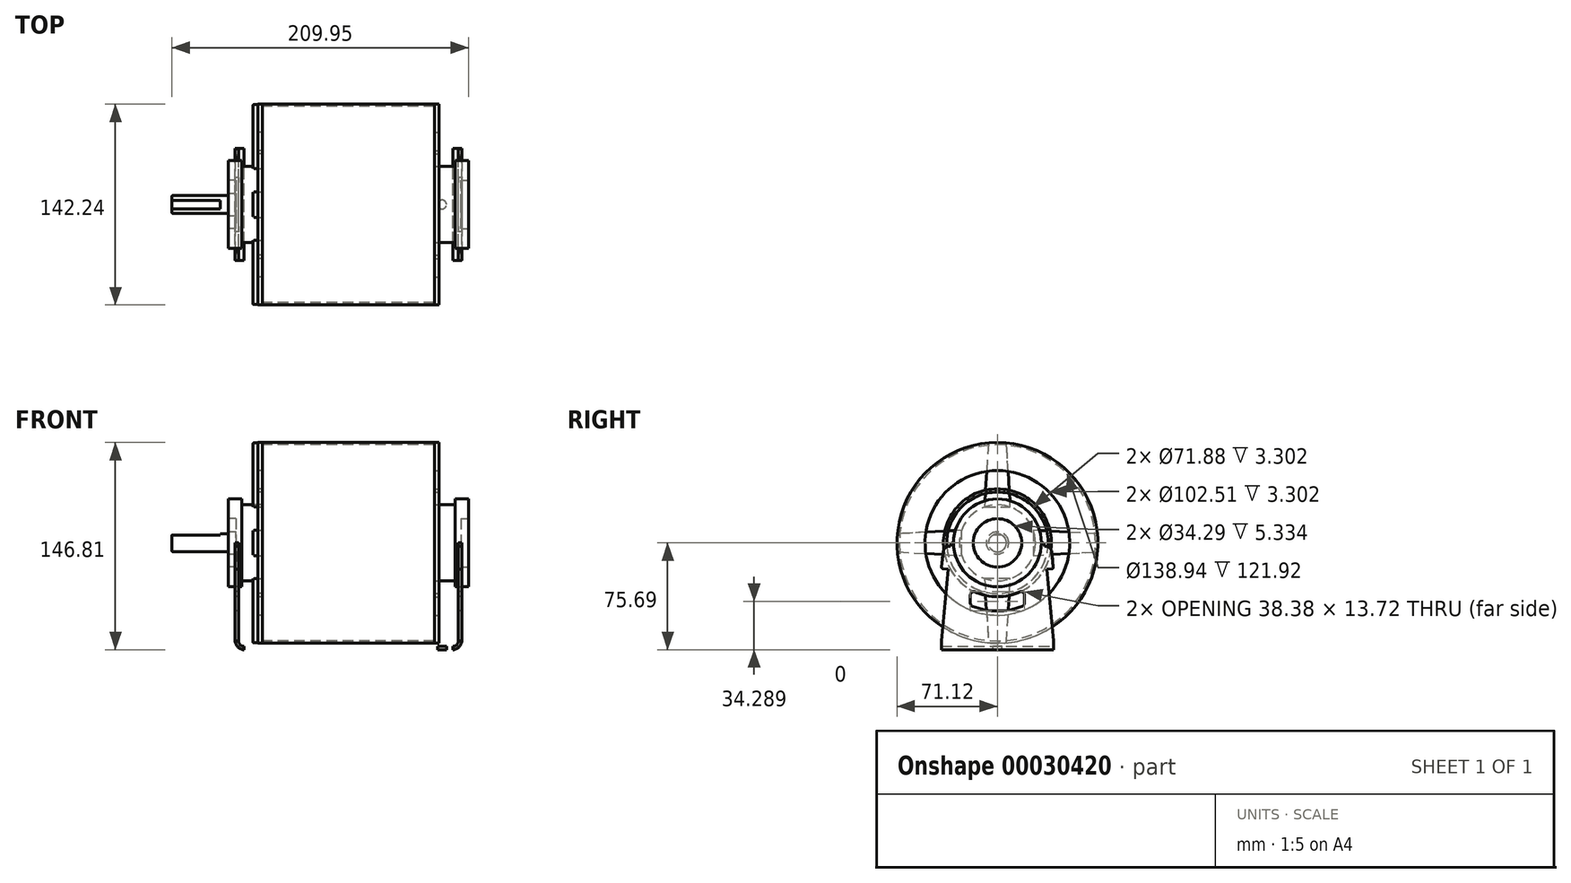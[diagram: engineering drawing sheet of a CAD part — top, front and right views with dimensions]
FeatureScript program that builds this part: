
annotation { "Feature Type Name" : "Feature", "Feature Type Description" : "" }
export const myFeature = defineFeature(function(context is Context, id is Id, definition is map)
    precondition{}
    {
        {
            var Q0;
            Q0=qCreatedBy(makeId("Right.planeOp"),FACE);
            var sketch = newSketch(context, id + "F0", { "sketchPlane" : qUnion([Q0])});
            skCircle(sketch, "E0", {"center": v(0, 0) * mm, "radius": 71.12 * mm});
            skCircle(sketch, "E1.0", {"center": v(0, 0) * mm, "radius": 69.47 * mm});
            skSolve(sketch);
        }
        {
            var Q0;
            Q0=makeQuery(id+"F0.imprint","IMPRINT",FACE,{"disambiguationData":[TD([[makeQuery(id+"F0.imprint","IMPRINT",EDGE,{"derivedFrom":sQuery(id+"F0.wireOp",EDGE,"E0")}),1.0]])]});
            extrude(context, id + "F1", {"entities" : qUnion([Q0]), "depth" : 121.92 * mm});
        }
        {
            var Q0;
            Q0=qCreatedBy(makeId("Front.planeOp"),FACE);
            var sketch = newSketch(context, id + "F2", { "sketchPlane" : qUnion([Q0])});
            skLineSegment(sketch, "E2", {"start": v(0, 0) * mm, "end": v(0, 71.12) * mm});
            skLineSegment(sketch, "E3", {"start": v(0, 71.12) * mm, "end": v(-3.3, 71.12) * mm});
            skLineSegment(sketch, "E4", {"start": v(-3.3, 71.12) * mm, "end": v(-3.3, 26.92) * mm});
            skLineSegment(sketch, "E5", {"start": v(-3.3, 26.92) * mm, "end": v(-14.48, 26.92) * mm});
            skLineSegment(sketch, "E6", {"start": v(-14.48, 26.92) * mm, "end": v(-14.48, 31.12) * mm});
            skLineSegment(sketch, "E7", {"start": v(-14.48, 31.12) * mm, "end": v(-24, 31.12) * mm});
            skLineSegment(sketch, "E8", {"start": v(-24, 31.12) * mm, "end": v(-24, 17.15) * mm});
            skLineSegment(sketch, "E9", {"start": v(-24, 17.15) * mm, "end": v(-18.67, 17.15) * mm});
            skLineSegment(sketch, "E10", {"start": v(-18.67, 17.15) * mm, "end": v(-18.67, 0) * mm});
            skLineSegment(sketch, "E11", {"start": v(-18.67, 0) * mm, "end": v(0, 0) * mm});
            skSolve(sketch);
        }
        {
            var Q0;
            Q0=makeQuery(id+"F2.imprint","IMPRINT",FACE,{"disambiguationData":[TD([[makeQuery(id+"F2.imprint","IMPRINT",EDGE,{"derivedFrom":sQuery(id+"F2.wireOp",EDGE,"E2")}),1.0]])]});
            var Q1;
            Q1=sQuery(id+"F2.wireOp",EDGE,"E11");
            revolve(context, id + "F3", {"entities" : qUnion([Q0]), "axis" : qUnion([Q1]), "revolveType" : RevolveType.FULL});
        }
        {
            var Q0;
            Q0=makeQuery(id+"F3.opRevolve","SWEPT_FACE",FACE,{"disambiguationData":[OSD([sQuery(id+"F2.wireOp",EDGE,"E4")])]});
            var sketch = newSketch(context, id + "F4", { "sketchPlane" : qUnion([Q0])});
            skCircle(sketch, "E12", {"center": v(0, 0) * mm, "radius": 51.26 * mm});
            skCircle(sketch, "E13", {"center": v(0, 0) * mm, "radius": 38.23 * mm});
            skCircle(sketch, "E14.0", {"center": v(0, 0) * mm, "radius": 35.94 * mm});
            skSolve(sketch);
        }
        {
            var Q0;
            Q0=qSketchRegion(id+"F4",true);
            var Q1;
            Q1=makeQuery(id+"F4.imprint","IMPRINT",FACE,{"disambiguationData":[TD([[makeQuery(id+"F4.imprint","IMPRINT",EDGE,{"derivedFrom":sQuery(id+"F4.wireOp",EDGE,"E14.0")}),1.0]])]});
            extrude(context, id + "F5", {"entities" : qUnion([Q0, Q1]), "operationType" : NewBodyOperationType.REMOVE, "endBound" : BoundingType.THROUGH_ALL, "oppositeDirection" : true, "depth" : 25.4 * mm});
        }
        {
            var Q0;
            Q0=qCreatedBy(makeId("Right.planeOp"),FACE);
            var sketch = newSketch(context, id + "F6", { "sketchPlane" : qUnion([Q0])});
            skLineSegment(sketch, "E15", {"start": v(0, 0) * mm, "end": v(0, 71.12) * mm, "construction": true});
            skPoint(sketch, "E16.rect.middle", {"position": v(0, 71.12) * mm});
            skCircle(sketch, "E17", {"center": v(0, 26.92) * mm, "radius": 9.2 * mm, "construction": true});
            skCircle(sketch, "E18.0", {"center": v(0, 0) * mm, "radius": 71.12 * mm, "construction": true});
            skCircle(sketch, "E19", {"center": v(0, 71.12) * mm, "radius": 6.35 * mm, "construction": true});
            skLineSegment(sketch, "E20", {"start": v(9.07, 25.35) * mm, "end": v(6.38, 70.83) * mm});
            skLineSegment(sketch, "E21", {"start": v(6.38, 70.83) * mm, "end": v(-6.38, 70.83) * mm});
            skLineSegment(sketch, "E22", {"start": v(-6.38, 70.83) * mm, "end": v(-9.07, 25.35) * mm});
            skLineSegment(sketch, "E23", {"start": v(-9.07, 25.35) * mm, "end": v(9.07, 25.35) * mm});
            skCircle(sketch, "E24.0", {"center": v(0, 0) * mm, "radius": 26.92 * mm, "construction": true});
            skSolve(sketch);
        }
        {
            var Q0;
            {var subQ3=sQuery(id+"F6.wireOp",EDGE,"E20");Q0=makeQuery(id+"F6.imprint","IMPRINT",FACE,{"disambiguationData":[TD([[makeQuery(id+"F6.imprint","IMPRINT",EDGE,{"derivedFrom":subQ3}),1.0]])]});}
            extrude(context, id + "F7", {"entities" : qUnion([Q0]), "oppositeDirection" : true, "depth" : 6.6 * mm});
        }
        {
            var Q0;
            Q0=makeQuery(id+"F7.opExtrude","CAP_EDGE",EDGE,{"disambiguationData":[OSD([sQuery(id+"F6.wireOp",EDGE,"E20")])],"isStart":false});
            var Q1;
            Q1=makeQuery(id+"F7.opExtrude","CAP_EDGE",EDGE,{"disambiguationData":[OSD([sQuery(id+"F6.wireOp",EDGE,"E21")])],"isStart":false});
            var Q2;
            Q2=makeQuery(id+"F7.opExtrude","CAP_EDGE",EDGE,{"disambiguationData":[OSD([sQuery(id+"F6.wireOp",EDGE,"E22")])],"isStart":false});
            var Q3;
            Q3=makeQuery(id+"F7.opExtrude","SWEPT_EDGE",EDGE,{"disambiguationData":[OSD([sQuery(id+"F2.wireOp",EDGE,"E3"),sQuery(id+"F2.wireOp",EDGE,"E4"),sQuery(id+"F6.wireOp",EDGE,"E20"),sQuery(id+"F6.wireOp",EDGE,"E21")])]});
            var Q4;
            Q4=makeQuery(id+"F7.opExtrude","SWEPT_EDGE",EDGE,{"disambiguationData":[OSD([sQuery(id+"F2.wireOp",EDGE,"E3"),sQuery(id+"F2.wireOp",EDGE,"E4"),sQuery(id+"F6.wireOp",EDGE,"E21"),sQuery(id+"F6.wireOp",EDGE,"E22")])]});
            fillet(context, id + "F8", {"entities" : qUnion([Q0, Q1, Q2, Q3, Q4]), "radius" : 0.5 * mm, "tangentPropagation" : true, "allowEdgeOverflow" : false});
        }
        {
            var Q0;
            Q0=makeQuery(id+"F7.opExtrude","SWEPT_BODY",BODY,{"disambiguationData":[OSD([sQuery(id+"F2.wireOp",EDGE,"E4"),sQuery(id+"F2.wireOp",EDGE,"E5"),sQuery(id+"F6.wireOp",EDGE,"E20"),sQuery(id+"F6.wireOp",EDGE,"E21"),sQuery(id+"F6.wireOp",EDGE,"E22")])]});
            var Q1;
            Q1=sQuery(id+"F2.wireOp",EDGE,"E11");
            circularPattern(context, id + "F9", {"entities" : qUnion([Q0]), "axis" : qUnion([Q1]), "angle" : 360 * degree, "instanceCount" : round(4), "equalSpace" : true});
        }
        {
            var Q0;
            Q0=qCreatedBy(makeId("Right.planeOp"),FACE);
            cPlane(context, id + "F10", {"entities" : qUnion([Q0]), "cplaneType" : CPlaneType.OFFSET, "offset" : 60.96 * mm, "width" : 152.4 * mm, "height" : 152.4 * mm});
        }
        {
            var Q0;
            Q0=makeQuery(id+"F5.boolean.opBoolean","SPLIT",BODY,{"disambiguationData":[OD(0.0)],"derivedFrom":makeQuery(id+"F3.opRevolve","SWEPT_BODY",BODY,{"disambiguationData":[OSD([sQuery(id+"F2.wireOp",EDGE,"E2"),sQuery(id+"F2.wireOp",EDGE,"E3"),sQuery(id+"F2.wireOp",EDGE,"E4"),sQuery(id+"F2.wireOp",EDGE,"E5"),sQuery(id+"F2.wireOp",EDGE,"E6"),sQuery(id+"F2.wireOp",EDGE,"E7"),sQuery(id+"F2.wireOp",EDGE,"E8"),sQuery(id+"F2.wireOp",EDGE,"E9"),sQuery(id+"F2.wireOp",EDGE,"E10"),sQuery(id+"F2.wireOp",EDGE,"E11")])]})});
            var Q1;
            Q1=qCreatedBy(id+"F10.planeOp",FACE);
            mirror(context, id + "F11", {"entities" : qUnion([Q0]), "mirrorPlane" : qUnion([Q1])});
        }
        {
            var Q0;
            Q0=qCreatedBy(makeId("Front.planeOp"),FACE);
            var sketch = newSketch(context, id + "F12", { "sketchPlane" : qUnion([Q0])});
            skLineSegment(sketch, "E25.0.0", {"start": v(-18.67, -17.15) * mm, "end": v(-18.67, 17.15) * mm, "construction": true});
            skLineSegment(sketch, "E26", {"start": v(-18.67, 0) * mm, "end": v(-64.03, 0) * mm});
            skLineSegment(sketch, "E27", {"start": v(-64.03, 0) * mm, "end": v(-64.03, 5.84) * mm});
            skLineSegment(sketch, "E28", {"start": v(-63.53, 6.35) * mm, "end": v(-23.75, 6.35) * mm});
            skLineSegment(sketch, "E29", {"start": v(-23.24, 7.89) * mm, "end": v(-18.67, 7.89) * mm});
            skLineSegment(sketch, "E30", {"start": v(-18.67, 7.89) * mm, "end": v(-18.67, 0) * mm});
            skLineSegment(sketch, "E31", {"start": v(-23.75, 7.38) * mm, "end": v(-23.75, 6.35) * mm});
            skPoint(sketch, "E32.visualSharp", {"position": v(-23.75, 7.89) * mm});
            skArc(sketch, "E32.filletArc", {"start": v(-23.24, 7.89) * mm, "mid": v(-23.6, 7.74) * mm, "end": v(-23.75, 7.38) * mm});
            skPoint(sketch, "E33.visualSharp", {"position": v(-64.03, 6.35) * mm});
            skArc(sketch, "E33.filletArc", {"start": v(-63.53, 6.35) * mm, "mid": v(-63.88, 6.2) * mm, "end": v(-64.03, 5.84) * mm});
            skSolve(sketch);
        }
        {
            var Q0;
            Q0=makeQuery(id+"F12.imprint","IMPRINT",FACE,{"disambiguationData":[TD([[makeQuery(id+"F12.imprint","IMPRINT",EDGE,{"derivedFrom":sQuery(id+"F12.wireOp",EDGE,"E26")}),-1.0]])]});
            var Q1;
            Q1=sQuery(id+"F12.wireOp",EDGE,"E26");
            revolve(context, id + "F13", {"entities" : qUnion([Q0]), "axis" : qUnion([Q1]), "revolveType" : RevolveType.FULL});
        }
        {
            var Q0;
            Q0=makeQuery(id+"F13.opRevolve","SWEPT_FACE",FACE,{"disambiguationData":[OSD([sQuery(id+"F12.wireOp",EDGE,"E27")])]});
            var sketch = newSketch(context, id + "F14", { "sketchPlane" : qUnion([Q0])});
            skCircle(sketch, "E34.0", {"center": v(0, 0) * mm, "radius": 6.35 * mm});
            skLineSegment(sketch, "E35", {"start": v(-6.6, -6.35) * mm, "end": v(6.6, -6.35) * mm, "construction": true});
            skLineSegment(sketch, "E36", {"start": v(0, -6.35) * mm, "end": v(0, 6.35) * mm, "construction": true});
            skLineSegment(sketch, "E37.0", {"start": v(-3.02, 5.59) * mm, "end": v(3.02, 5.59) * mm});
            skSolve(sketch);
        }
        {
            var Q0;
            {var subQ0=makeQuery(id+"F13.opRevolve","SWEPT_EDGE",EDGE,{"disambiguationData":[OSD([sQuery(id+"F12.wireOp",EDGE,"E27"),sQuery(id+"F12.wireOp",EDGE,"E33.filletArc")])]});var subQ1=sQuery(id+"F14.wireOp",EDGE,"E37.0");var subQ3=makeQuery(id+"F14.imprint","INTERSECT",VERTEX,{"disambiguationData":[OD(0.0)],"derivedFrom":[subQ0,subQ1]});Q0=makeQuery(id+"F14.imprint","IMPRINT",FACE,{"disambiguationData":[TD([[makeQuery(id+"F14.imprint","IMPRINT",EDGE,{"disambiguationData":[TD([[subQ3,-1.0]])],"derivedFrom":subQ1}),1.0]])]});}
            var Q1;
            {var subQ1=sQuery(id+"F14.wireOp",EDGE,"E37.0");var subQ4=sQuery(id+"F14.wireOp",EDGE,"E34.0");var subQ6=makeQuery(id+"F14.imprint","INTERSECT",VERTEX,{"disambiguationData":[OD(0.0)],"derivedFrom":[subQ4,subQ1]});Q1=makeQuery(id+"F14.imprint","IMPRINT",FACE,{"disambiguationData":[TD([[makeQuery(id+"F14.imprint","IMPRINT",EDGE,{"disambiguationData":[TD([[subQ6,1.0]])],"derivedFrom":subQ4}),1.0]])]});}
            extrude(context, id + "F15", {"entities" : qUnion([Q0, Q1]), "operationType" : NewBodyOperationType.REMOVE, "oppositeDirection" : true, "depth" : 34.04 * mm});
        }
        {
            var Q0;
            Q0=qCreatedBy(makeId("Front.planeOp"),FACE);
            var sketch = newSketch(context, id + "F16", { "sketchPlane" : qUnion([Q0])});
            skLineSegment(sketch, "E38", {"start": v(-154.25, 0) * mm, "end": v(252.33, 0) * mm, "construction": true});
            skLineSegment(sketch, "E39", {"start": v(-12.9, -75.7) * mm, "end": v(134.81, -75.7) * mm});
            skLineSegment(sketch, "E40", {"start": v(-24, 31.12) * mm, "end": v(-14.48, 31.12) * mm, "construction": true});
            skLineSegment(sketch, "E41", {"start": v(136.4, 31.12) * mm, "end": v(145.92, 31.12) * mm, "construction": true});
            skLineSegment(sketch, "E42", {"start": v(-19.24, 31.12) * mm, "end": v(-19.24, 0) * mm, "construction": true});
            skLineSegment(sketch, "E43", {"start": v(141.16, 31.12) * mm, "end": v(141.16, 0) * mm, "construction": true});
            skLineSegment(sketch, "E44", {"start": v(-19.24, 0) * mm, "end": v(-19.24, -69.34) * mm});
            skLineSegment(sketch, "E45", {"start": v(141.16, 0) * mm, "end": v(141.16, -69.34) * mm});
            skPoint(sketch, "E46.visualSharp", {"position": v(-19.24, -75.7) * mm});
            skArc(sketch, "E46.filletArc", {"start": v(-19.24, -69.34) * mm, "mid": v(-17.38, -73.83) * mm, "end": v(-12.9, -75.7) * mm});
            skPoint(sketch, "E47.visualSharp", {"position": v(141.16, -75.7) * mm});
            skArc(sketch, "E47.filletArc", {"start": v(134.81, -75.7) * mm, "mid": v(139.3, -73.83) * mm, "end": v(141.16, -69.34) * mm});
            skLineSegment(sketch, "E48.0", {"start": v(138.87, 0) * mm, "end": v(138.87, -69.34) * mm});
            skArc(sketch, "E48.1", {"start": v(134.81, -73.4) * mm, "mid": v(137.68, -72.22) * mm, "end": v(138.87, -69.34) * mm});
            skLineSegment(sketch, "E48.2", {"start": v(-12.9, -73.4) * mm, "end": v(134.81, -73.4) * mm});
            skArc(sketch, "E48.3", {"start": v(-16.95, -69.34) * mm, "mid": v(-15.76, -72.22) * mm, "end": v(-12.9, -73.4) * mm});
            skLineSegment(sketch, "E48.4", {"start": v(-16.95, 0) * mm, "end": v(-16.95, -69.34) * mm});
            skLineSegment(sketch, "E49", {"start": v(-19.24, 0) * mm, "end": v(-16.95, 0) * mm});
            skLineSegment(sketch, "E50", {"start": v(138.87, 0) * mm, "end": v(141.16, 0) * mm});
            skSolve(sketch);
        }
        {
            var Q0;
            Q0=qSketchRegion(id+"F16",true);
            extrude(context, id + "F17", {"entities" : qUnion([Q0]), "endBound" : BoundingType.SYMMETRIC, "depth" : 79.5 * mm});
        }
        {
            var Q0;
            Q0=qCreatedBy(makeId("Top.planeOp"),FACE);
            cPlane(context, id + "F18", {"entities" : qUnion([Q0]), "cplaneType" : CPlaneType.OFFSET, "offset" : 75.7 * mm, "oppositeDirection" : true, "width" : 152.4 * mm, "height" : 152.4 * mm});
        }
        {
            var Q0;
            Q0=qCreatedBy(id+"F18.planeOp",FACE);
            var sketch = newSketch(context, id + "F19", { "sketchPlane" : qUnion([Q0])});
            skLineSegment(sketch, "E51.0", {"start": v(-19.24, -39.75) * mm, "end": v(-12.9, -39.75) * mm, "construction": true});
            skLineSegment(sketch, "E52.0", {"start": v(-19.24, 39.75) * mm, "end": v(-12.9, 39.75) * mm, "construction": true});
            skLineSegment(sketch, "E53.bottom", {"start": v(15.34, 66.04) * mm, "end": v(15.34, 66.04) * mm});
            skLineSegment(sketch, "E53.top", {"start": v(15.34, 40.64) * mm, "end": v(15.34, 40.64) * mm});
            skLineSegment(sketch, "E53.left", {"start": v(11.37, 62.07) * mm, "end": v(11.37, 44.6) * mm});
            skLineSegment(sketch, "E53.right", {"start": v(19.3, 62.07) * mm, "end": v(19.3, 44.6) * mm});
            skPoint(sketch, "E54.visualSharp", {"position": v(11.37, 66.04) * mm});
            skArc(sketch, "E54.filletArc", {"start": v(15.34, 66.04) * mm, "mid": v(12.53, 64.88) * mm, "end": v(11.37, 62.07) * mm});
            skPoint(sketch, "E55.visualSharp", {"position": v(19.3, 66.04) * mm});
            skArc(sketch, "E55.filletArc", {"start": v(19.3, 62.07) * mm, "mid": v(18.14, 64.88) * mm, "end": v(15.34, 66.04) * mm});
            skPoint(sketch, "E56.visualSharp", {"position": v(19.3, 40.64) * mm});
            skArc(sketch, "E56.filletArc", {"start": v(15.34, 40.64) * mm, "mid": v(18.14, 41.8) * mm, "end": v(19.3, 44.6) * mm});
            skPoint(sketch, "E57.visualSharp", {"position": v(11.37, 40.64) * mm});
            skArc(sketch, "E57.filletArc", {"start": v(11.37, 44.6) * mm, "mid": v(12.53, 41.8) * mm, "end": v(15.34, 40.64) * mm});
            skLineSegment(sketch, "E58", {"start": v(2.98, 39.75) * mm, "end": v(2.98, -39.75) * mm, "construction": true});
            skLineSegment(sketch, "E59", {"start": v(-19.24, 0) * mm, "end": v(141.16, 0) * mm, "construction": true});
            skLineSegment(sketch, "E60", {"start": v(9.33, 71.5) * mm, "end": v(111.68, 71.5) * mm});
            skLineSegment(sketch, "E61", {"start": v(9.33, -71.5) * mm, "end": v(111.68, -71.5) * mm});
            skLineSegment(sketch, "E62", {"start": v(2.98, 46.1) * mm, "end": v(2.98, 65.15) * mm});
            skLineSegment(sketch, "E63", {"start": v(2.98, -46.1) * mm, "end": v(2.98, -65.15) * mm});
            skLineSegment(sketch, "E64", {"start": v(-19.24, 39.75) * mm, "end": v(-19.24, -39.75) * mm, "construction": true});
            skLineSegment(sketch, "E65.0", {"start": v(141.16, -39.75) * mm, "end": v(141.16, 39.75) * mm, "construction": true});
            skLineSegment(sketch, "E66", {"start": v(141.16, 39.75) * mm, "end": v(134.81, 39.75) * mm, "construction": true});
            skLineSegment(sketch, "E67", {"start": v(126.25, 45.4) * mm, "end": v(117.6, 67.47) * mm});
            skPoint(sketch, "E68.visualSharp", {"position": v(128.46, 39.75) * mm});
            skArc(sketch, "E68.filletArc", {"start": v(126.25, 45.4) * mm, "mid": v(129.51, 41.3) * mm, "end": v(134.52, 39.75) * mm});
            skPoint(sketch, "E69.visualSharp", {"position": v(2.98, 71.5) * mm});
            skArc(sketch, "E69.filletArc", {"start": v(9.33, 71.5) * mm, "mid": v(4.84, 69.64) * mm, "end": v(2.98, 65.15) * mm});
            skLineSegment(sketch, "E70.0.MirrorCS", {"start": v(141.16, -39.75) * mm, "end": v(134.81, -39.75) * mm, "construction": true});
            skLineSegment(sketch, "E70.1.MirrorCS", {"start": v(126.25, -45.4) * mm, "end": v(117.6, -67.47) * mm});
            skArc(sketch, "E70.2.MirrorCS", {"start": v(126.25, -45.4) * mm, "mid": v(129.51, -41.3) * mm, "end": v(134.52, -39.75) * mm});
            skPoint(sketch, "E71.visualSharp", {"position": v(116.01, 71.5) * mm});
            skArc(sketch, "E71.filletArc", {"start": v(117.6, 67.47) * mm, "mid": v(115.26, 70.4) * mm, "end": v(111.68, 71.5) * mm});
            skPoint(sketch, "E72.visualSharp", {"position": v(116.01, -71.5) * mm});
            skArc(sketch, "E72.filletArc", {"start": v(111.68, -71.5) * mm, "mid": v(115.26, -70.4) * mm, "end": v(117.6, -67.47) * mm});
            skPoint(sketch, "E73.visualSharp", {"position": v(2.98, -71.5) * mm});
            skArc(sketch, "E73.filletArc", {"start": v(2.98, -65.15) * mm, "mid": v(4.84, -69.64) * mm, "end": v(9.33, -71.5) * mm});
            skPoint(sketch, "E74.visualSharp", {"position": v(2.98, 39.75) * mm});
            skArc(sketch, "E74.filletArc", {"start": v(-3.37, 39.75) * mm, "mid": v(1.12, 41.61) * mm, "end": v(2.98, 46.1) * mm});
            skPoint(sketch, "E75.visualSharp", {"position": v(2.98, -39.75) * mm});
            skArc(sketch, "E75.filletArc", {"start": v(2.98, -46.1) * mm, "mid": v(1.12, -41.61) * mm, "end": v(-3.37, -39.75) * mm});
            skArc(sketch, "E76.0.1.0", {"start": v(15.34, -66.04) * mm, "mid": v(18.14, -64.88) * mm, "end": v(19.3, -62.07) * mm});
            skArc(sketch, "E76.0.1.1", {"start": v(11.37, -62.07) * mm, "mid": v(12.53, -64.88) * mm, "end": v(15.34, -66.04) * mm});
            skLineSegment(sketch, "E76.0.1.2", {"start": v(11.37, -44.6) * mm, "end": v(11.37, -62.07) * mm});
            skArc(sketch, "E76.0.1.3", {"start": v(15.34, -40.64) * mm, "mid": v(12.53, -41.8) * mm, "end": v(11.37, -44.6) * mm});
            skArc(sketch, "E76.0.1.4", {"start": v(19.3, -44.6) * mm, "mid": v(18.14, -41.8) * mm, "end": v(15.34, -40.64) * mm});
            skLineSegment(sketch, "E76.0.1.5", {"start": v(19.3, -44.6) * mm, "end": v(19.3, -62.07) * mm});
            skArc(sketch, "E76.1.0.0", {"start": v(83.92, 40.64) * mm, "mid": v(86.72, 41.8) * mm, "end": v(87.88, 44.6) * mm});
            skArc(sketch, "E76.1.0.1", {"start": v(79.95, 44.6) * mm, "mid": v(81.1, 41.8) * mm, "end": v(83.92, 40.64) * mm});
            skLineSegment(sketch, "E76.1.0.2", {"start": v(79.95, 62.07) * mm, "end": v(79.95, 44.6) * mm});
            skArc(sketch, "E76.1.0.3", {"start": v(83.92, 66.04) * mm, "mid": v(81.1, 64.88) * mm, "end": v(79.95, 62.07) * mm});
            skArc(sketch, "E76.1.0.4", {"start": v(87.88, 62.07) * mm, "mid": v(86.72, 64.88) * mm, "end": v(83.92, 66.04) * mm});
            skLineSegment(sketch, "E76.1.0.5", {"start": v(87.88, 62.07) * mm, "end": v(87.88, 44.6) * mm});
            skArc(sketch, "E76.1.1.0", {"start": v(83.92, -66.04) * mm, "mid": v(86.72, -64.88) * mm, "end": v(87.88, -62.07) * mm});
            skArc(sketch, "E76.1.1.1", {"start": v(79.95, -62.07) * mm, "mid": v(81.1, -64.88) * mm, "end": v(83.92, -66.04) * mm});
            skLineSegment(sketch, "E76.1.1.2", {"start": v(79.95, -44.6) * mm, "end": v(79.95, -62.07) * mm});
            skArc(sketch, "E76.1.1.3", {"start": v(83.92, -40.64) * mm, "mid": v(81.1, -41.8) * mm, "end": v(79.95, -44.6) * mm});
            skArc(sketch, "E76.1.1.4", {"start": v(87.88, -44.6) * mm, "mid": v(86.72, -41.8) * mm, "end": v(83.92, -40.64) * mm});
            skLineSegment(sketch, "E76.1.1.5", {"start": v(87.88, -44.6) * mm, "end": v(87.88, -62.07) * mm});
            skLineSegment(sketch, "E76.direction1", {"start": v(15.34, 40.64) * mm, "end": v(83.92, 40.64) * mm, "construction": true});
            skLineSegment(sketch, "E76.direction2", {"start": v(15.34, 40.64) * mm, "end": v(15.34, -66.04) * mm, "construction": true});
            skLineSegment(sketch, "E77.0", {"start": v(-12.9, -39.75) * mm, "end": v(-12.9, 39.75) * mm});
            skLineSegment(sketch, "E78.0", {"start": v(134.81, -39.75) * mm, "end": v(134.81, 39.75) * mm});
            skLineSegment(sketch, "E79", {"start": v(-12.9, 39.75) * mm, "end": v(-3.37, 39.75) * mm});
            skLineSegment(sketch, "E80", {"start": v(-12.9, -39.75) * mm, "end": v(-3.37, -39.75) * mm});
            skLineSegment(sketch, "E81", {"start": v(134.81, 39.75) * mm, "end": v(134.52, 39.75) * mm});
            skLineSegment(sketch, "E82", {"start": v(134.81, -39.75) * mm, "end": v(134.52, -39.75) * mm});
            skSolve(sketch);
        }
        {
            var Q0;
            Q0=makeQuery(id+"F19.imprint","IMPRINT",FACE,{"disambiguationData":[TD([[makeQuery(id+"F19.imprint","IMPRINT",EDGE,{"derivedFrom":sQuery(id+"F19.wireOp",EDGE,"E53.left")}),-1.0]])]});
            extrude(context, id + "F20", {"entities" : qUnion([Q0]), "operationType" : NewBodyOperationType.ADD, "depth" : 2.3 * mm});
        }
        {
            var Q0;
            Q0=makeQuery(id+"F17.opExtrude","SWEPT_FACE",FACE,{"disambiguationData":[OSD([sQuery(id+"F16.wireOp",EDGE,"E44")])]});
            var sketch = newSketch(context, id + "F21", { "sketchPlane" : qUnion([Q0])});
            skArc(sketch, "E83.0", {"start": v(-31.12, 0) * mm, "mid": v(0, -31.12) * mm, "end": v(31.12, 0) * mm});
            skLineSegment(sketch, "E84.0", {"start": v(39.75, -69.34) * mm, "end": v(-39.75, -69.34) * mm});
            skLineSegment(sketch, "E85", {"start": v(31.87, 0) * mm, "end": v(31.12, 0) * mm});
            skLineSegment(sketch, "E86", {"start": v(-33.13, -1.15) * mm, "end": v(-39.75, -69.34) * mm});
            skLineSegment(sketch, "E87", {"start": v(33.13, -1.15) * mm, "end": v(39.75, -69.34) * mm});
            skPoint(sketch, "E88.end.orphan", {"position": v(-39.75, 0) * mm});
            skPoint(sketch, "E89.0.start.orphan", {"position": v(39.75, 0) * mm});
            skLineSegment(sketch, "E90.trimOffspring", {"start": v(-31.12, 0) * mm, "end": v(-31.87, 0) * mm});
            skLineSegment(sketch, "E91", {"start": v(0, 0) * mm, "end": v(0, -69.34) * mm, "construction": true});
            skPoint(sketch, "E92.visualSharp", {"position": v(-33.02, 0) * mm});
            skArc(sketch, "E92.filletArc", {"start": v(-31.87, 0) * mm, "mid": v(-32.72, -0.33) * mm, "end": v(-33.13, -1.15) * mm});
            skPoint(sketch, "E93.visualSharp", {"position": v(33.02, 0) * mm});
            skArc(sketch, "E93.filletArc", {"start": v(33.13, -1.15) * mm, "mid": v(32.72, -0.33) * mm, "end": v(31.87, 0) * mm});
            skLineSegment(sketch, "E94.bottom", {"start": v(33.27, -2.6) * mm, "end": v(33.78, -2.55) * mm});
            skLineSegment(sketch, "E94.top", {"start": v(34.84, -18.78) * mm, "end": v(38.38, -18.44) * mm});
            skLineSegment(sketch, "E94.left", {"start": v(33.27, -2.6) * mm, "end": v(34.84, -18.78) * mm});
            skLineSegment(sketch, "E94.right", {"start": v(38.5, -6.43) * mm, "end": v(39.52, -17.05) * mm});
            skPoint(sketch, "E95.visualSharp", {"position": v(38.08, -2.13) * mm});
            skArc(sketch, "E95.filletArc", {"start": v(38.5, -6.43) * mm, "mid": v(36.94, -3.51) * mm, "end": v(33.78, -2.55) * mm});
            skPoint(sketch, "E96.visualSharp", {"position": v(39.65, -18.31) * mm});
            skArc(sketch, "E96.filletArc", {"start": v(38.38, -18.44) * mm, "mid": v(39.24, -17.98) * mm, "end": v(39.52, -17.05) * mm});
            skLineSegment(sketch, "E97.0.MirrorCS", {"start": v(-33.27, -2.6) * mm, "end": v(-33.78, -2.55) * mm});
            skArc(sketch, "E97.1.MirrorCS", {"start": v(-38.5, -6.43) * mm, "mid": v(-36.94, -3.51) * mm, "end": v(-33.78, -2.55) * mm});
            skLineSegment(sketch, "E97.2.MirrorCS", {"start": v(-34.84, -18.78) * mm, "end": v(-38.38, -18.44) * mm});
            skLineSegment(sketch, "E97.3.MirrorCS", {"start": v(-38.5, -6.43) * mm, "end": v(-39.52, -17.05) * mm});
            skArc(sketch, "E97.4.MirrorCS", {"start": v(-38.38, -18.44) * mm, "mid": v(-39.24, -17.98) * mm, "end": v(-39.52, -17.05) * mm});
            skArc(sketch, "E98", {"start": v(-15.6, -34.76) * mm, "mid": v(0, -38.1) * mm, "end": v(15.6, -34.76) * mm});
            skArc(sketch, "E99.0", {"start": v(-17.57, -44.95) * mm, "mid": v(0, -48.26) * mm, "end": v(17.57, -44.95) * mm});
            skLineSegment(sketch, "E100.rect.left", {"start": v(19.19, -37.07) * mm, "end": v(19.19, -42.58) * mm});
            skLineSegment(sketch, "E100.rect.right", {"start": v(-19.19, -37.07) * mm, "end": v(-19.19, -42.58) * mm});
            skPoint(sketch, "E100.rect.middle", {"position": v(0, -43.18) * mm});
            skPoint(sketch, "E101.orphan", {"position": v(-19.19, -53.44) * mm});
            skPoint(sketch, "E100.rect.top.start.orphan", {"position": v(19.19, -53.44) * mm});
            skPoint(sketch, "E102.visualSharp", {"position": v(-19.19, -44.28) * mm});
            skArc(sketch, "E102.filletArc", {"start": v(-19.19, -42.58) * mm, "mid": v(-18.75, -44.01) * mm, "end": v(-17.57, -44.95) * mm});
            skPoint(sketch, "E103.visualSharp", {"position": v(19.19, -44.28) * mm});
            skArc(sketch, "E103.filletArc", {"start": v(17.57, -44.95) * mm, "mid": v(18.75, -44.01) * mm, "end": v(19.19, -42.58) * mm});
            skPoint(sketch, "E104.visualSharp", {"position": v(19.19, -32.92) * mm});
            skArc(sketch, "E104.filletArc", {"start": v(19.19, -37.07) * mm, "mid": v(18.03, -34.94) * mm, "end": v(15.6, -34.76) * mm});
            skPoint(sketch, "E105.visualSharp", {"position": v(-19.19, -32.92) * mm});
            skArc(sketch, "E105.filletArc", {"start": v(-15.6, -34.76) * mm, "mid": v(-18.03, -34.94) * mm, "end": v(-19.19, -37.07) * mm});
            skSolve(sketch);
        }
        {
            var Q0;
            {var subQ2=sQuery(id+"F21.wireOp",EDGE,"E92.filletArc");Q0=makeQuery(id+"F21.imprint","IMPRINT",FACE,{"disambiguationData":[TD([[makeQuery(id+"F21.imprint","IMPRINT",EDGE,{"derivedFrom":subQ2}),-1.0]])]});}
            var Q1;
            {var subQ2=sQuery(id+"F21.wireOp",EDGE,"E93.filletArc");Q1=makeQuery(id+"F21.imprint","IMPRINT",FACE,{"disambiguationData":[TD([[makeQuery(id+"F21.imprint","IMPRINT",EDGE,{"derivedFrom":subQ2}),-1.0]])]});}
            var Q2;
            {var subQ1=sQuery(id+"F21.wireOp",EDGE,"E83.0");Q2=makeQuery(id+"F21.imprint","IMPRINT",FACE,{"disambiguationData":[TD([[makeQuery(id+"F21.imprint","IMPRINT",EDGE,{"derivedFrom":subQ1}),1.0]])]});}
            var Q3;
            Q3=makeQuery(id+"F21.imprint","IMPRINT",FACE,{"disambiguationData":[TD([[makeQuery(id+"F21.imprint","IMPRINT",EDGE,{"derivedFrom":sQuery(id+"F21.wireOp",EDGE,"E98")}),-1.0]])]});
            extrude(context, id + "F22", {"entities" : qUnion([Q0, Q1, Q2, Q3]), "oppositeDirection" : true, "depth" : 160.4 * mm});
        }
        {
            var Q0;
            Q0=makeQuery(id+"F22.opExtrude","SWEPT_BODY",BODY,{"disambiguationData":[OSD([sQuery(id+"F16.wireOp",EDGE,"E44"),sQuery(id+"F16.wireOp",EDGE,"E49"),sQuery(id+"F21.wireOp",EDGE,"E83.0")])]});
            var Q1;
            Q1=makeQuery(id+"F22.opExtrude","SWEPT_BODY",BODY,{"disambiguationData":[OSD([sQuery(id+"F16.wireOp",EDGE,"E44"),sQuery(id+"F16.wireOp",EDGE,"E49"),sQuery(id+"F21.wireOp",EDGE,"E86"),sQuery(id+"F21.wireOp",EDGE,"E92.filletArc"),sQuery(id+"F21.wireOp",EDGE,"E97.0.MirrorCS"),sQuery(id+"F21.wireOp",EDGE,"E97.1.MirrorCS"),sQuery(id+"F21.wireOp",EDGE,"E97.2.MirrorCS"),sQuery(id+"F21.wireOp",EDGE,"E97.3.MirrorCS"),sQuery(id+"F21.wireOp",EDGE,"E97.4.MirrorCS")])]});
            var Q2;
            Q2=makeQuery(id+"F22.opExtrude","SWEPT_BODY",BODY,{"disambiguationData":[OSD([sQuery(id+"F16.wireOp",EDGE,"E44"),sQuery(id+"F16.wireOp",EDGE,"E49"),sQuery(id+"F21.wireOp",EDGE,"E87"),sQuery(id+"F21.wireOp",EDGE,"E93.filletArc"),sQuery(id+"F21.wireOp",EDGE,"E94.bottom"),sQuery(id+"F21.wireOp",EDGE,"E94.top"),sQuery(id+"F21.wireOp",EDGE,"E94.right"),sQuery(id+"F21.wireOp",EDGE,"E95.filletArc"),sQuery(id+"F21.wireOp",EDGE,"E96.filletArc")])]});
            var Q3;
            Q3=makeQuery(id+"F22.opExtrude","SWEPT_BODY",BODY,{"disambiguationData":[OSD([sQuery(id+"F21.wireOp",EDGE,"E98"),sQuery(id+"F21.wireOp",EDGE,"E99.0"),sQuery(id+"F21.wireOp",EDGE,"E100.rect.left"),sQuery(id+"F21.wireOp",EDGE,"E100.rect.right"),sQuery(id+"F21.wireOp",EDGE,"E102.filletArc"),sQuery(id+"F21.wireOp",EDGE,"E103.filletArc"),sQuery(id+"F21.wireOp",EDGE,"E104.filletArc"),sQuery(id+"F21.wireOp",EDGE,"E105.filletArc")])]});
            var Q4;
            Q4=makeQuery(id+"F17.opExtrude","SWEPT_BODY",BODY,{"disambiguationData":[OSD([sQuery(id+"F16.wireOp",EDGE,"E39"),sQuery(id+"F16.wireOp",EDGE,"E44"),sQuery(id+"F16.wireOp",EDGE,"E45"),sQuery(id+"F16.wireOp",EDGE,"E46.filletArc"),sQuery(id+"F16.wireOp",EDGE,"E47.filletArc"),sQuery(id+"F16.wireOp",EDGE,"E48.0"),sQuery(id+"F16.wireOp",EDGE,"E48.1"),sQuery(id+"F16.wireOp",EDGE,"E48.2"),sQuery(id+"F16.wireOp",EDGE,"E48.3"),sQuery(id+"F16.wireOp",EDGE,"E48.4"),sQuery(id+"F16.wireOp",EDGE,"E49"),sQuery(id+"F16.wireOp",EDGE,"E50")])]});
            booleanBodies(context, id + "F23", {"operationType" : BooleanOperationType.SUBTRACTION, "tools" : qUnion([Q0, Q1, Q2, Q3]), "targets" : qUnion([Q4])});
        }
        {
            var Q0;
            Q0=makeQuery(id+"F20.boolean.opBoolean","MERGE",FACE,{"derivedFrom":[makeQuery(id+"F17.opExtrude","SWEPT_FACE",FACE,{"disambiguationData":[OSD([sQuery(id+"F16.wireOp",EDGE,"E48.2")])]}),makeQuery(id+"F20.opExtrude","CAP_FACE",FACE,{"disambiguationData":[OSD([sQuery(id+"F19.wireOp",EDGE,"E53.left"),sQuery(id+"F19.wireOp",EDGE,"E53.right"),sQuery(id+"F19.wireOp",EDGE,"E54.filletArc"),sQuery(id+"F19.wireOp",EDGE,"E55.filletArc"),sQuery(id+"F19.wireOp",EDGE,"E56.filletArc"),sQuery(id+"F19.wireOp",EDGE,"E57.filletArc"),sQuery(id+"F19.wireOp",EDGE,"E60"),sQuery(id+"F19.wireOp",EDGE,"E61"),sQuery(id+"F19.wireOp",EDGE,"E62"),sQuery(id+"F19.wireOp",EDGE,"E63"),sQuery(id+"F19.wireOp",EDGE,"E67"),sQuery(id+"F19.wireOp",EDGE,"E68.filletArc"),sQuery(id+"F19.wireOp",EDGE,"E69.filletArc"),sQuery(id+"F19.wireOp",EDGE,"E70.1.MirrorCS"),sQuery(id+"F19.wireOp",EDGE,"E70.2.MirrorCS"),sQuery(id+"F19.wireOp",EDGE,"E71.filletArc"),sQuery(id+"F19.wireOp",EDGE,"E72.filletArc"),sQuery(id+"F19.wireOp",EDGE,"E73.filletArc"),sQuery(id+"F19.wireOp",EDGE,"E74.filletArc"),sQuery(id+"F19.wireOp",EDGE,"E75.filletArc"),sQuery(id+"F19.wireOp",EDGE,"E76.0.1.0"),sQuery(id+"F19.wireOp",EDGE,"E76.0.1.1"),sQuery(id+"F19.wireOp",EDGE,"E76.0.1.2"),sQuery(id+"F19.wireOp",EDGE,"E76.0.1.3"),sQuery(id+"F19.wireOp",EDGE,"E76.0.1.4"),sQuery(id+"F19.wireOp",EDGE,"E76.0.1.5"),sQuery(id+"F19.wireOp",EDGE,"E76.1.0.0"),sQuery(id+"F19.wireOp",EDGE,"E76.1.0.1"),sQuery(id+"F19.wireOp",EDGE,"E76.1.0.2"),sQuery(id+"F19.wireOp",EDGE,"E76.1.0.3"),sQuery(id+"F19.wireOp",EDGE,"E76.1.0.4"),sQuery(id+"F19.wireOp",EDGE,"E76.1.0.5"),sQuery(id+"F19.wireOp",EDGE,"E76.1.1.0"),sQuery(id+"F19.wireOp",EDGE,"E76.1.1.1"),sQuery(id+"F19.wireOp",EDGE,"E76.1.1.2"),sQuery(id+"F19.wireOp",EDGE,"E76.1.1.3"),sQuery(id+"F19.wireOp",EDGE,"E76.1.1.4"),sQuery(id+"F19.wireOp",EDGE,"E76.1.1.5"),sQuery(id+"F19.wireOp",EDGE,"E77.0"),sQuery(id+"F19.wireOp",EDGE,"E78.0"),sQuery(id+"F19.wireOp",EDGE,"E79"),sQuery(id+"F19.wireOp",EDGE,"E80"),sQuery(id+"F19.wireOp",EDGE,"E81"),sQuery(id+"F19.wireOp",EDGE,"E82")])],"isStart":false})]});
            var sketch = newSketch(context, id + "F24", { "sketchPlane" : qUnion([Q0])});
            skLineSegment(sketch, "E106.0", {"start": v(-12.9, -39.75) * mm, "end": v(-12.9, 39.75) * mm, "construction": true});
            skLineSegment(sketch, "E107.0", {"start": v(134.81, -39.75) * mm, "end": v(134.81, 39.75) * mm, "construction": true});
            skLineSegment(sketch, "E108.rect.bottom", {"start": v(4.89, 7.62) * mm, "end": v(117.03, 7.62) * mm});
            skLineSegment(sketch, "E108.rect.top", {"start": v(4.89, -7.62) * mm, "end": v(117.03, -7.62) * mm});
            skLineSegment(sketch, "E108.rect.left", {"start": v(2.35, 5.08) * mm, "end": v(2.35, -5.08) * mm});
            skLineSegment(sketch, "E108.rect.right", {"start": v(119.57, 5.08) * mm, "end": v(119.57, -5.08) * mm});
            skPoint(sketch, "E108.rect.middle", {"position": v(60.96, 0) * mm});
            skLineSegment(sketch, "E109", {"start": v(2.35, 0) * mm, "end": v(-12.9, 0) * mm, "construction": true});
            skLineSegment(sketch, "E110", {"start": v(119.57, 0) * mm, "end": v(134.81, 0) * mm, "construction": true});
            skCircle(sketch, "E111", {"center": v(-5.27, 0) * mm, "radius": 3.18 * mm});
            skLineSegment(sketch, "E112", {"start": v(60.96, 7.62) * mm, "end": v(60.96, -7.62) * mm, "construction": true});
            skCircle(sketch, "E113.0.MirrorC", {"center": v(127.2, 0) * mm, "radius": 3.18 * mm});
            skPoint(sketch, "E114.visualSharp", {"position": v(2.35, 7.62) * mm});
            skArc(sketch, "E114.filletArc", {"start": v(4.89, 7.62) * mm, "mid": v(3.1, 6.88) * mm, "end": v(2.35, 5.08) * mm});
            skPoint(sketch, "E115.visualSharp", {"position": v(119.57, 7.62) * mm});
            skArc(sketch, "E115.filletArc", {"start": v(119.57, 5.08) * mm, "mid": v(118.83, 6.88) * mm, "end": v(117.03, 7.62) * mm});
            skPoint(sketch, "E116.visualSharp", {"position": v(119.57, -7.62) * mm});
            skArc(sketch, "E116.filletArc", {"start": v(117.03, -7.62) * mm, "mid": v(118.83, -6.88) * mm, "end": v(119.57, -5.08) * mm});
            skPoint(sketch, "E117.visualSharp", {"position": v(2.35, -7.62) * mm});
            skArc(sketch, "E117.filletArc", {"start": v(2.35, -5.08) * mm, "mid": v(3.1, -6.88) * mm, "end": v(4.89, -7.62) * mm});
            skSolve(sketch);
        }
        {
            var Q0;
            Q0=makeQuery(id+"F24.imprint","IMPRINT",FACE,{"disambiguationData":[TD([[makeQuery(id+"F24.imprint","IMPRINT",EDGE,{"derivedFrom":sQuery(id+"F24.wireOp",EDGE,"E111")}),1.0]])]});
            var Q1;
            Q1=makeQuery(id+"F24.imprint","IMPRINT",FACE,{"disambiguationData":[TD([[makeQuery(id+"F24.imprint","IMPRINT",EDGE,{"derivedFrom":sQuery(id+"F24.wireOp",EDGE,"E108.rect.bottom")}),-1.0]])]});
            var Q2;
            Q2=makeQuery(id+"F24.imprint","IMPRINT",FACE,{"disambiguationData":[TD([[makeQuery(id+"F24.imprint","IMPRINT",EDGE,{"derivedFrom":sQuery(id+"F24.wireOp",EDGE,"E113.0.MirrorC")}),-1.0]])]});
            extrude(context, id + "F25", {"entities" : qUnion([Q0, Q1, Q2]), "operationType" : NewBodyOperationType.REMOVE, "endBound" : BoundingType.THROUGH_ALL, "oppositeDirection" : true, "depth" : 25.4 * mm});
        }
    });
